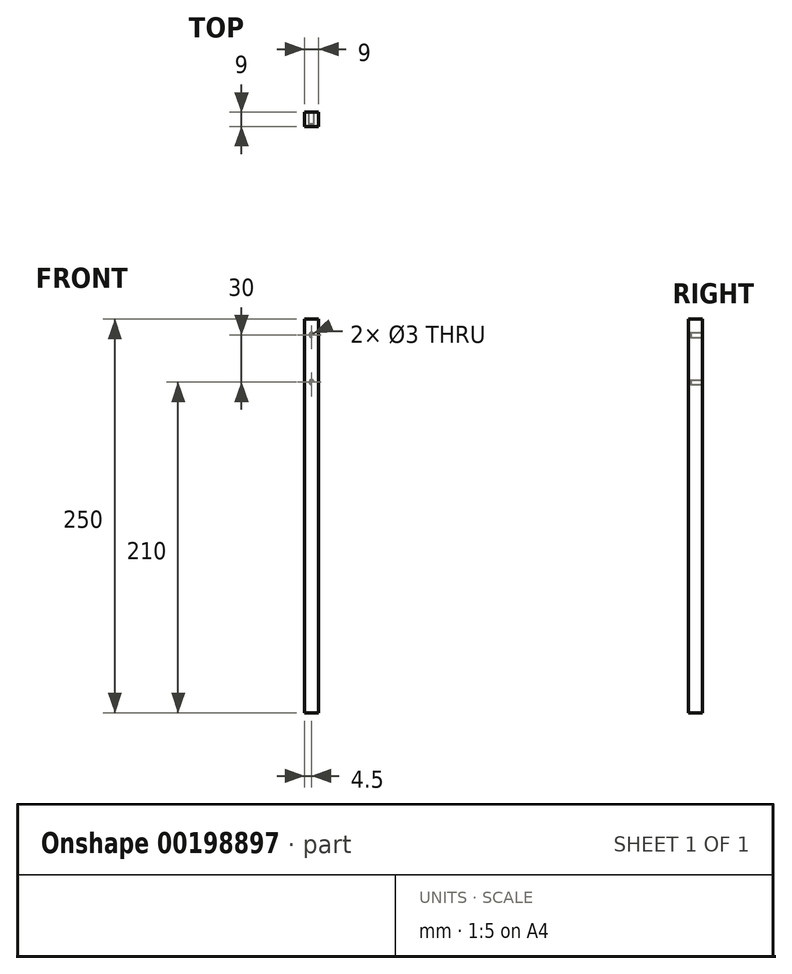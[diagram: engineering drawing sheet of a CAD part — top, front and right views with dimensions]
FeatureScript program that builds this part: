
annotation { "Feature Type Name" : "Feature", "Feature Type Description" : "" }
export const myFeature = defineFeature(function(context is Context, id is Id, definition is map)
    precondition{}
    {
        {
            var Q0;
            Q0=qCreatedBy(makeId("Top.planeOp"),FACE);
            var sketch = newSketch(context, id + "F0", { "sketchPlane" : qUnion([Q0])});
            skLineSegment(sketch, "E0.bottom", {"start": v(4.5, 4.5) * mm, "end": v(-4.5, 4.5) * mm});
            skLineSegment(sketch, "E0.top", {"start": v(4.5, -4.5) * mm, "end": v(-4.5, -4.5) * mm});
            skLineSegment(sketch, "E0.left", {"start": v(4.5, 4.5) * mm, "end": v(4.5, -4.5) * mm});
            skLineSegment(sketch, "E0.right", {"start": v(-4.5, 4.5) * mm, "end": v(-4.5, -4.5) * mm});
            skPoint(sketch, "E0.middle", {"position": v(0, 0) * mm});
            skSolve(sketch);
        }
        {
            var Q0;
            Q0=makeQuery(id+"F0.imprint","IMPRINT",FACE,{"disambiguationData":[TD([[makeQuery(id+"F0.imprint","IMPRINT",EDGE,{"derivedFrom":sQuery(id+"F0.wireOp",EDGE,"E0.bottom")}),1.0]])]});
            extrude(context, id + "F1", {"entities" : qUnion([Q0]), "depth" : 250 * mm});
        }
        {
            var Q0;
            Q0=makeQuery(id+"F1.opExtrude","SWEPT_FACE",FACE,{"disambiguationData":[OSD([sQuery(id+"F0.wireOp",EDGE,"E0.bottom")])]});
            var sketch = newSketch(context, id + "F2", { "sketchPlane" : qUnion([Q0])});
            skPoint(sketch, "E1", {"position": v(0, 240) * mm});
            skPoint(sketch, "E2", {"position": v(0, 210) * mm});
            skSolve(sketch);
        }
        {
            var Q0;
            Q0=sQuery(id+"F2.wireOp",VERTEX,"E1");
            var Q1;
            Q1=sQuery(id+"F2.wireOp",VERTEX,"E2");
            var Q2;
            Q2=makeQuery(id+"F1.opExtrude","SWEPT_BODY",BODY,{"disambiguationData":[OSD([sQuery(id+"F0.wireOp",EDGE,"E0.bottom"),sQuery(id+"F0.wireOp",EDGE,"E0.top"),sQuery(id+"F0.wireOp",EDGE,"E0.left"),sQuery(id+"F0.wireOp",EDGE,"E0.right")])]});
            hole(context, id + "F3", {"style" : HoleStyle.SIMPLE, "endStyle" : HoleEndStyle.BLIND, "holeDiameter" : 3 * mm, "holeDepth" : 7.5 * mm, "startFromSketch" : true, "locations" : qUnion([Q0, Q1]), "scope" : qUnion([Q2])});
        }
    });
